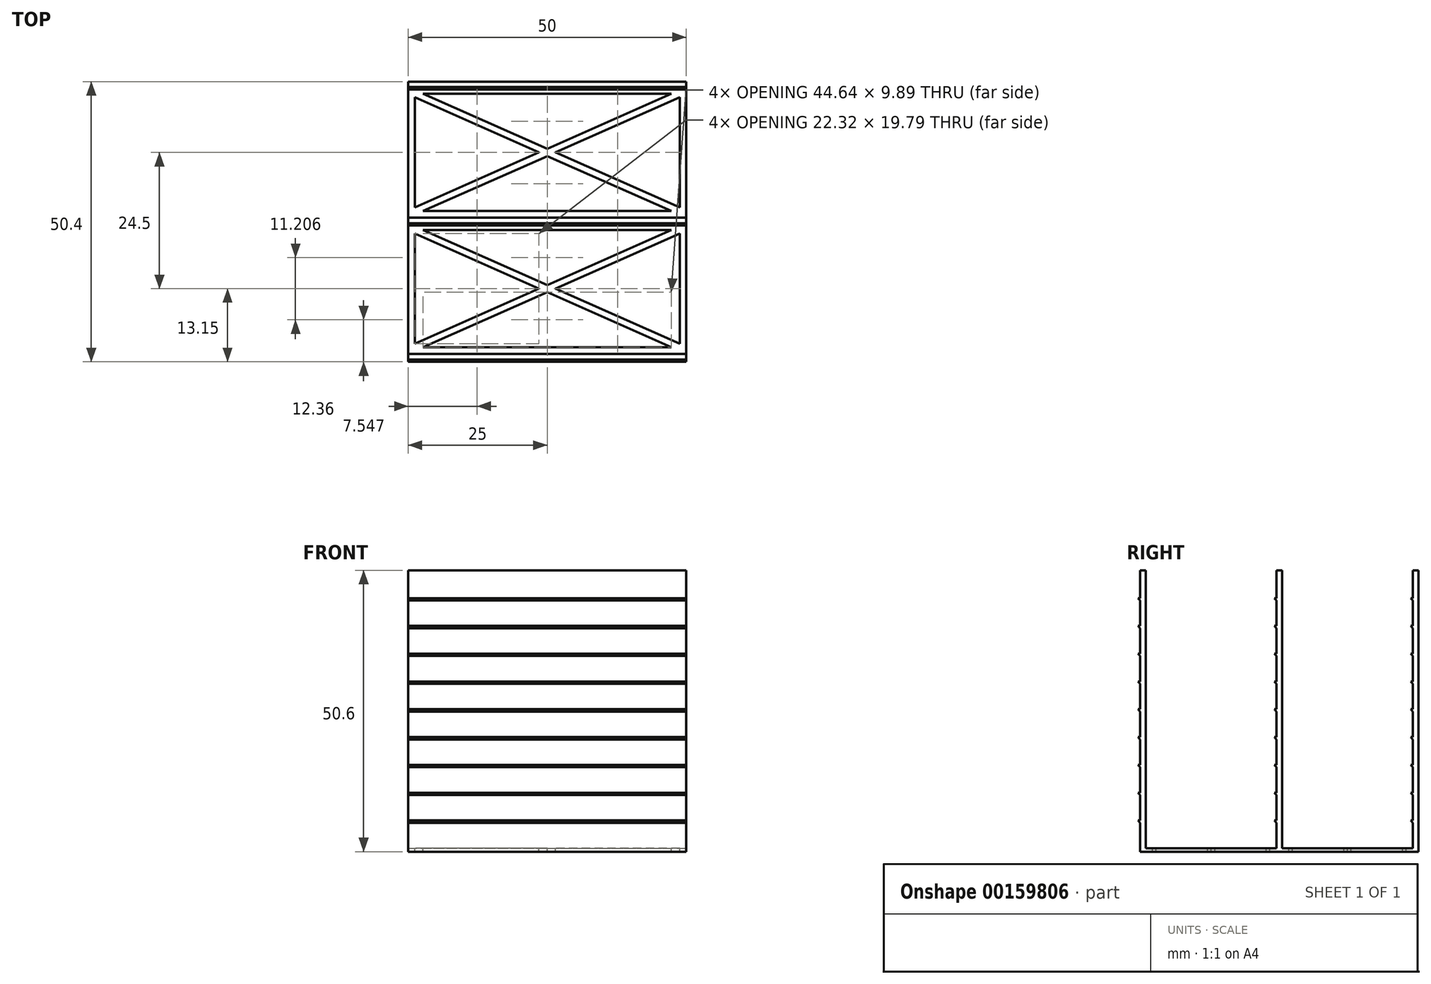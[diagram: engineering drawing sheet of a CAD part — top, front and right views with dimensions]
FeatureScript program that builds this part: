
annotation { "Feature Type Name" : "Feature", "Feature Type Description" : "" }
export const myFeature = defineFeature(function(context is Context, id is Id, definition is map)
    precondition{}
    {
        {
            var Q0;
            Q0=qCreatedBy(makeId("Top.planeOp"),FACE);
            var sketch = newSketch(context, id + "F0", { "sketchPlane" : qUnion([Q0])});
            skPoint(sketch, "E0.middle", {"position": v(0, 0) * mm});
            skLineSegment(sketch, "E1.bottom", {"start": v(-25, 25) * mm, "end": v(25, 25) * mm});
            skLineSegment(sketch, "E1.top", {"start": v(-25, 24) * mm, "end": v(25, 24) * mm});
            skLineSegment(sketch, "E1.left", {"start": v(-25, 25) * mm, "end": v(-25, 24) * mm});
            skLineSegment(sketch, "E1.right", {"start": v(25, 25) * mm, "end": v(25, 24) * mm});
            skPoint(sketch, "E1.middle", {"position": v(0, 24.5) * mm});
            skLineSegment(sketch, "E2.bottom", {"start": v(-25, 0.5) * mm, "end": v(25, 0.5) * mm});
            skLineSegment(sketch, "E2.top", {"start": v(-25, -0.5) * mm, "end": v(25, -0.5) * mm});
            skLineSegment(sketch, "E2.left", {"start": v(-25, 0.5) * mm, "end": v(-25, -0.5) * mm});
            skLineSegment(sketch, "E2.right", {"start": v(25, 0.5) * mm, "end": v(25, -0.5) * mm});
            skLineSegment(sketch, "E3.bottom", {"start": v(-25, -24) * mm, "end": v(25, -24) * mm});
            skLineSegment(sketch, "E3.top", {"start": v(-25, -25) * mm, "end": v(25, -25) * mm});
            skLineSegment(sketch, "E3.left", {"start": v(-25, -24) * mm, "end": v(-25, -25) * mm});
            skLineSegment(sketch, "E3.right", {"start": v(25, -24) * mm, "end": v(25, -25) * mm});
            skPoint(sketch, "E3.middle", {"position": v(0, -24.5) * mm});
            skLineSegment(sketch, "E4.left", {"start": v(-25, 25) * mm, "end": v(-25, -25) * mm});
            skLineSegment(sketch, "E4.right", {"start": v(25, 25) * mm, "end": v(25, -25) * mm});
            skLineSegment(sketch, "E5.bottom", {"start": v(-23.8, 22.8) * mm, "end": v(23.8, 22.8) * mm});
            skLineSegment(sketch, "E5.top", {"start": v(-23.8, 1.7) * mm, "end": v(23.8, 1.7) * mm});
            skLineSegment(sketch, "E5.left", {"start": v(-23.8, 22.8) * mm, "end": v(-23.8, 1.7) * mm});
            skLineSegment(sketch, "E5.right", {"start": v(23.8, 22.8) * mm, "end": v(23.8, 1.7) * mm});
            skLineSegment(sketch, "E6", {"start": v(-23.8, 22.8) * mm, "end": v(23.8, 1.7) * mm, "construction": true});
            skLineSegment(sketch, "E7", {"start": v(23.8, 22.8) * mm, "end": v(-23.8, 1.7) * mm, "construction": true});
            skLineSegment(sketch, "E8", {"start": v(-23.8, 22.8) * mm, "end": v(-25, 22.8) * mm, "construction": true});
            skLineSegment(sketch, "E9", {"start": v(-23.8, 22.8) * mm, "end": v(-23.8, 24) * mm, "construction": true});
            skLineSegment(sketch, "E10", {"start": v(-23.8, 1.7) * mm, "end": v(-23.8, 0.5) * mm, "construction": true});
            skLineSegment(sketch, "E11.0", {"start": v(-23.8, 22.14) * mm, "end": v(22.32, 1.7) * mm});
            skLineSegment(sketch, "E12.0", {"start": v(-22.32, 22.8) * mm, "end": v(23.8, 2.36) * mm});
            skLineSegment(sketch, "E13.0", {"start": v(22.32, 22.8) * mm, "end": v(-23.8, 2.36) * mm});
            skLineSegment(sketch, "E14.0", {"start": v(23.8, 22.14) * mm, "end": v(-22.32, 1.7) * mm});
            skLineSegment(sketch, "E15.MirrorCS", {"start": v(-23.8, -22.8) * mm, "end": v(-23.8, -1.7) * mm});
            skLineSegment(sketch, "E16.MirrorCS", {"start": v(-23.8, -1.7) * mm, "end": v(23.8, -1.7) * mm});
            skLineSegment(sketch, "E17.MirrorCS", {"start": v(23.8, -22.8) * mm, "end": v(23.8, -1.7) * mm});
            skLineSegment(sketch, "E18.MirrorCS", {"start": v(-23.8, -22.8) * mm, "end": v(23.8, -22.8) * mm});
            skLineSegment(sketch, "E19.MirrorCS", {"start": v(23.8, -22.14) * mm, "end": v(-22.32, -1.7) * mm});
            skLineSegment(sketch, "E20.MirrorCS", {"start": v(22.32, -22.8) * mm, "end": v(-23.8, -2.36) * mm});
            skLineSegment(sketch, "E21.MirrorCS", {"start": v(-22.32, -22.8) * mm, "end": v(23.8, -2.36) * mm});
            skLineSegment(sketch, "E22.MirrorCS", {"start": v(-23.8, -22.14) * mm, "end": v(22.32, -1.7) * mm});
            skSolve(sketch);
        }
        {
            var Q0;
            Q0=makeQuery(id+"F0.imprint","IMPRINT",FACE,{"disambiguationData":[TD([[makeQuery(id+"F0.imprint","IMPRINT",EDGE,{"derivedFrom":sQuery(id+"F0.wireOp",EDGE,"E0.bottom")}),1.0]])]});
            var Q1;
            Q1=makeQuery(id+"F0.imprint","IMPRINT",FACE,{"disambiguationData":[TD([[makeQuery(id+"F0.imprint","IMPRINT",EDGE,{"derivedFrom":sQuery(id+"F0.wireOp",EDGE,"QWfyO98P-nReG-di9y-126s-5mOLykfiqYH5")}),1.0]])]});
            var Q2;
            Q2=makeQuery(id+"F0.imprint","IMPRINT",FACE,{"disambiguationData":[TD([[makeQuery(id+"F0.imprint","IMPRINT",EDGE,{"derivedFrom":sQuery(id+"F0.wireOp",EDGE,"DmCEL1rD-3tOg-Wg76-rsYw-25NWHVf6hnsO")}),1.0]])]});
            var Q3;
            Q3=makeQuery(id+"F0.imprint","IMPRINT",FACE,{"disambiguationData":[TD([[makeQuery(id+"F0.imprint","IMPRINT",EDGE,{"derivedFrom":sQuery(id+"F0.wireOp",EDGE,"K1cKH9qt-eAHN-jujT-Ysw8-32v16pyBWlPN")}),1.0]])]});
            var Q4;
            Q4=makeQuery(id+"F0.imprint","IMPRINT",FACE,{"disambiguationData":[TD([[makeQuery(id+"F0.imprint","IMPRINT",EDGE,{"derivedFrom":sQuery(id+"F0.wireOp",EDGE,"bcf984ff-cba1-42ba-802e-a5a17bfec991.0.1.2")}),1.0]])]});
            var Q5;
            Q5=makeQuery(id+"F0.imprint","IMPRINT",FACE,{"disambiguationData":[TD([[makeQuery(id+"F0.imprint","IMPRINT",EDGE,{"derivedFrom":sQuery(id+"F0.wireOp",EDGE,"bcf984ff-cba1-42ba-802e-a5a17bfec991.0.1.1")}),1.0]])]});
            var Q6;
            Q6=makeQuery(id+"F0.imprint","IMPRINT",FACE,{"disambiguationData":[TD([[makeQuery(id+"F0.imprint","IMPRINT",EDGE,{"derivedFrom":sQuery(id+"F0.wireOp",EDGE,"bcf984ff-cba1-42ba-802e-a5a17bfec991.0.1.0")}),1.0]])]});
            var Q7;
            Q7=makeQuery(id+"F0.imprint","IMPRINT",FACE,{"disambiguationData":[TD([[makeQuery(id+"F0.imprint","IMPRINT",EDGE,{"derivedFrom":sQuery(id+"F0.wireOp",EDGE,"bcf984ff-cba1-42ba-802e-a5a17bfec991.0.2.0")}),1.0]])]});
            var Q8;
            Q8=makeQuery(id+"F0.imprint","IMPRINT",FACE,{"disambiguationData":[TD([[makeQuery(id+"F0.imprint","IMPRINT",EDGE,{"derivedFrom":sQuery(id+"F0.wireOp",EDGE,"bcf984ff-cba1-42ba-802e-a5a17bfec991.0.2.1")}),1.0]])]});
            var Q9;
            Q9=makeQuery(id+"F0.imprint","IMPRINT",FACE,{"disambiguationData":[TD([[makeQuery(id+"F0.imprint","IMPRINT",EDGE,{"derivedFrom":sQuery(id+"F0.wireOp",EDGE,"bcf984ff-cba1-42ba-802e-a5a17bfec991.0.2.2")}),1.0]])]});
            var Q10;
            {var subQ0=sQuery(id+"F0.wireOp",EDGE,"E1.top");Q10=makeQuery(id+"F0.imprint","IMPRINT",FACE,{"disambiguationData":[TD([[makeQuery(id+"F0.imprint","IMPRINT",EDGE,{"derivedFrom":subQ0}),-1.0]])]});}
            var Q11;
            {var subQ0=sQuery(id+"F0.wireOp",EDGE,"E2.top");Q11=makeQuery(id+"F0.imprint","IMPRINT",FACE,{"disambiguationData":[TD([[makeQuery(id+"F0.imprint","IMPRINT",EDGE,{"derivedFrom":subQ0}),-1.0]])]});}
            var Q12;
            {var subQ0=sQuery(id+"F0.wireOp",EDGE,"E3.bottom");Q12=makeQuery(id+"F0.imprint","IMPRINT",FACE,{"disambiguationData":[TD([[makeQuery(id+"F0.imprint","IMPRINT",EDGE,{"derivedFrom":subQ0}),-1.0]])]});}
            var Q13;
            {var subQ0=sQuery(id+"F0.wireOp",EDGE,"E2.bottom");Q13=makeQuery(id+"F0.imprint","IMPRINT",FACE,{"disambiguationData":[TD([[makeQuery(id+"F0.imprint","IMPRINT",EDGE,{"derivedFrom":subQ0}),-1.0]])]});}
            var Q14;
            {var subQ0=sQuery(id+"F0.wireOp",EDGE,"E1.top");Q14=makeQuery(id+"F0.imprint","IMPRINT",FACE,{"disambiguationData":[TD([[makeQuery(id+"F0.imprint","IMPRINT",EDGE,{"derivedFrom":subQ0}),1.0]])]});}
            var Q15;
            {var subQ1=sQuery(id+"F0.wireOp",EDGE,"E5.bottom");var subQ6=sQuery(id+"F0.wireOp",EDGE,"E5.left");var subQ9=makeQuery(id+"F0.imprint","INTERSECT",VERTEX,{"derivedFrom":[subQ1,subQ6]});Q15=makeQuery(id+"F0.imprint","IMPRINT",FACE,{"disambiguationData":[TD([[makeQuery(id+"F0.imprint","IMPRINT",EDGE,{"disambiguationData":[TD([[subQ9,-1.0]])],"derivedFrom":subQ1}),-1.0]])]});}
            var Q16;
            {var subQ1=sQuery(id+"F0.wireOp",EDGE,"E5.bottom");var subQ5=sQuery(id+"F0.wireOp",EDGE,"E5.right");var subQ6=makeQuery(id+"F0.imprint","INTERSECT",VERTEX,{"derivedFrom":[subQ1,subQ5]});Q16=makeQuery(id+"F0.imprint","IMPRINT",FACE,{"disambiguationData":[TD([[makeQuery(id+"F0.imprint","IMPRINT",EDGE,{"disambiguationData":[TD([[subQ6,1.0]])],"derivedFrom":subQ1}),-1.0]])]});}
            var Q17;
            {var subQ0=sQuery(id+"F0.wireOp",EDGE,"E13.0");var subQ1=sQuery(id+"F0.wireOp",EDGE,"E11.0");var subQ2=makeQuery(id+"F0.imprint","INTERSECT",VERTEX,{"derivedFrom":[subQ1,subQ0]});Q17=makeQuery(id+"F0.imprint","IMPRINT",FACE,{"disambiguationData":[TD([[makeQuery(id+"F0.imprint","IMPRINT",EDGE,{"disambiguationData":[TD([[subQ2,-1.0]])],"derivedFrom":subQ1}),1.0]])]});}
            var Q18;
            {var subQ1=sQuery(id+"F0.wireOp",EDGE,"E5.right");var subQ6=sQuery(id+"F0.wireOp",EDGE,"E5.top");var subQ9=makeQuery(id+"F0.imprint","INTERSECT",VERTEX,{"derivedFrom":[subQ6,subQ1]});Q18=makeQuery(id+"F0.imprint","IMPRINT",FACE,{"disambiguationData":[TD([[makeQuery(id+"F0.imprint","IMPRINT",EDGE,{"disambiguationData":[TD([[subQ9,1.0]])],"derivedFrom":subQ6}),1.0]])]});}
            var Q19;
            {var subQ5=sQuery(id+"F0.wireOp",EDGE,"E5.left");var subQ6=sQuery(id+"F0.wireOp",EDGE,"E5.top");var subQ7=makeQuery(id+"F0.imprint","INTERSECT",VERTEX,{"derivedFrom":[subQ6,subQ5]});Q19=makeQuery(id+"F0.imprint","IMPRINT",FACE,{"disambiguationData":[TD([[makeQuery(id+"F0.imprint","IMPRINT",EDGE,{"disambiguationData":[TD([[subQ7,-1.0]])],"derivedFrom":subQ6}),1.0]])]});}
            var Q20;
            {var subQ1=sQuery(id+"F0.wireOp",EDGE,"E16.MirrorCS");var subQ6=sQuery(id+"F0.wireOp",EDGE,"E15.MirrorCS");var subQ9=makeQuery(id+"F0.imprint","INTERSECT",VERTEX,{"derivedFrom":[subQ6,subQ1]});Q20=makeQuery(id+"F0.imprint","IMPRINT",FACE,{"disambiguationData":[TD([[makeQuery(id+"F0.imprint","IMPRINT",EDGE,{"disambiguationData":[TD([[subQ9,1.0]])],"derivedFrom":subQ6}),-1.0]])]});}
            var Q21;
            {var subQ0=sQuery(id+"F0.wireOp",EDGE,"E21.MirrorCS");var subQ1=sQuery(id+"F0.wireOp",EDGE,"E19.MirrorCS");var subQ2=makeQuery(id+"F0.imprint","INTERSECT",VERTEX,{"derivedFrom":[subQ1,subQ0]});Q21=makeQuery(id+"F0.imprint","IMPRINT",FACE,{"disambiguationData":[TD([[makeQuery(id+"F0.imprint","IMPRINT",EDGE,{"disambiguationData":[TD([[subQ2,-1.0]])],"derivedFrom":subQ1}),1.0]])]});}
            var Q22;
            {var subQ5=sQuery(id+"F0.wireOp",EDGE,"E17.MirrorCS");var subQ6=sQuery(id+"F0.wireOp",EDGE,"E16.MirrorCS");var subQ7=makeQuery(id+"F0.imprint","INTERSECT",VERTEX,{"derivedFrom":[subQ6,subQ5]});Q22=makeQuery(id+"F0.imprint","IMPRINT",FACE,{"disambiguationData":[TD([[makeQuery(id+"F0.imprint","IMPRINT",EDGE,{"disambiguationData":[TD([[subQ7,1.0]])],"derivedFrom":subQ6}),-1.0]])]});}
            var Q23;
            {var subQ1=sQuery(id+"F0.wireOp",EDGE,"E18.MirrorCS");var subQ6=sQuery(id+"F0.wireOp",EDGE,"E17.MirrorCS");var subQ9=makeQuery(id+"F0.imprint","INTERSECT",VERTEX,{"derivedFrom":[subQ6,subQ1]});Q23=makeQuery(id+"F0.imprint","IMPRINT",FACE,{"disambiguationData":[TD([[makeQuery(id+"F0.imprint","IMPRINT",EDGE,{"disambiguationData":[TD([[subQ9,-1.0]])],"derivedFrom":subQ6}),1.0]])]});}
            var Q24;
            {var subQ1=sQuery(id+"F0.wireOp",EDGE,"E18.MirrorCS");var subQ5=sQuery(id+"F0.wireOp",EDGE,"E15.MirrorCS");var subQ6=makeQuery(id+"F0.imprint","INTERSECT",VERTEX,{"derivedFrom":[subQ5,subQ1]});Q24=makeQuery(id+"F0.imprint","IMPRINT",FACE,{"disambiguationData":[TD([[makeQuery(id+"F0.imprint","IMPRINT",EDGE,{"disambiguationData":[TD([[subQ6,-1.0]])],"derivedFrom":subQ5}),-1.0]])]});}
            extrude(context, id + "F1", {"entities" : qUnion([Q0, Q1, Q2, Q3, Q4, Q5, Q6, Q7, Q8, Q9, Q10, Q11, Q12, Q13, Q14, Q15, Q16, Q17, Q18, Q19, Q20, Q21, Q22, Q23, Q24]), "oppositeDirection" : true, "depth" : 0.6 * mm});
        }
        {
            var Q0;
            Q0=makeQuery(id+"F0.imprint","IMPRINT",FACE,{"disambiguationData":[TD([[makeQuery(id+"F0.imprint","IMPRINT",EDGE,{"derivedFrom":sQuery(id+"F0.wireOp",EDGE,"QWfyO98P-nReG-di9y-126s-5mOLykfiqYH5")}),1.0]])]});
            var Q1;
            Q1=makeQuery(id+"F0.imprint","IMPRINT",FACE,{"disambiguationData":[TD([[makeQuery(id+"F0.imprint","IMPRINT",EDGE,{"derivedFrom":sQuery(id+"F0.wireOp",EDGE,"DmCEL1rD-3tOg-Wg76-rsYw-25NWHVf6hnsO")}),1.0]])]});
            var Q2;
            Q2=makeQuery(id+"F0.imprint","IMPRINT",FACE,{"disambiguationData":[TD([[makeQuery(id+"F0.imprint","IMPRINT",EDGE,{"derivedFrom":sQuery(id+"F0.wireOp",EDGE,"K1cKH9qt-eAHN-jujT-Ysw8-32v16pyBWlPN")}),1.0]])]});
            var Q3;
            Q3=makeQuery(id+"F0.imprint","IMPRINT",FACE,{"disambiguationData":[TD([[makeQuery(id+"F0.imprint","IMPRINT",EDGE,{"derivedFrom":sQuery(id+"F0.wireOp",EDGE,"bcf984ff-cba1-42ba-802e-a5a17bfec991.0.1.2")}),1.0]])]});
            var Q4;
            Q4=makeQuery(id+"F0.imprint","IMPRINT",FACE,{"disambiguationData":[TD([[makeQuery(id+"F0.imprint","IMPRINT",EDGE,{"derivedFrom":sQuery(id+"F0.wireOp",EDGE,"bcf984ff-cba1-42ba-802e-a5a17bfec991.0.1.1")}),1.0]])]});
            var Q5;
            Q5=makeQuery(id+"F0.imprint","IMPRINT",FACE,{"disambiguationData":[TD([[makeQuery(id+"F0.imprint","IMPRINT",EDGE,{"derivedFrom":sQuery(id+"F0.wireOp",EDGE,"bcf984ff-cba1-42ba-802e-a5a17bfec991.0.1.0")}),1.0]])]});
            var Q6;
            Q6=makeQuery(id+"F0.imprint","IMPRINT",FACE,{"disambiguationData":[TD([[makeQuery(id+"F0.imprint","IMPRINT",EDGE,{"derivedFrom":sQuery(id+"F0.wireOp",EDGE,"bcf984ff-cba1-42ba-802e-a5a17bfec991.0.2.0")}),1.0]])]});
            var Q7;
            Q7=makeQuery(id+"F0.imprint","IMPRINT",FACE,{"disambiguationData":[TD([[makeQuery(id+"F0.imprint","IMPRINT",EDGE,{"derivedFrom":sQuery(id+"F0.wireOp",EDGE,"bcf984ff-cba1-42ba-802e-a5a17bfec991.0.2.1")}),1.0]])]});
            var Q8;
            Q8=makeQuery(id+"F0.imprint","IMPRINT",FACE,{"disambiguationData":[TD([[makeQuery(id+"F0.imprint","IMPRINT",EDGE,{"derivedFrom":sQuery(id+"F0.wireOp",EDGE,"bcf984ff-cba1-42ba-802e-a5a17bfec991.0.2.2")}),1.0]])]});
            var Q9;
            {var subQ0=sQuery(id+"F0.wireOp",EDGE,"E1.top");Q9=makeQuery(id+"F0.imprint","IMPRINT",FACE,{"disambiguationData":[TD([[makeQuery(id+"F0.imprint","IMPRINT",EDGE,{"derivedFrom":subQ0}),1.0]])]});}
            var Q10;
            {var subQ0=sQuery(id+"F0.wireOp",EDGE,"E2.bottom");Q10=makeQuery(id+"F0.imprint","IMPRINT",FACE,{"disambiguationData":[TD([[makeQuery(id+"F0.imprint","IMPRINT",EDGE,{"derivedFrom":subQ0}),-1.0]])]});}
            var Q11;
            {var subQ0=sQuery(id+"F0.wireOp",EDGE,"E3.bottom");Q11=makeQuery(id+"F0.imprint","IMPRINT",FACE,{"disambiguationData":[TD([[makeQuery(id+"F0.imprint","IMPRINT",EDGE,{"derivedFrom":subQ0}),-1.0]])]});}
            extrude(context, id + "F2", {"entities" : qUnion([Q0, Q1, Q2, Q3, Q4, Q5, Q6, Q7, Q8, Q9, Q10, Q11]), "operationType" : NewBodyOperationType.ADD, "depth" : 50 * mm});
        }
        {
            var Q0;
            {var subQ0=sQuery(id+"F0.wireOp",EDGE,"E4.left");Q0=makeQuery(id+"F2.boolean.opBoolean","MERGE",FACE,{"derivedFrom":[makeQuery(id+"F1.opExtrude","SWEPT_FACE",FACE,{"disambiguationData":[OSD([subQ0])]}),makeQuery(id+"F2.opExtrude","SWEPT_FACE",FACE,{"disambiguationData":[OSD([subQ0]),TDD([makeQuery(id+"F0.imprint","IMPRINT",EDGE,{"disambiguationData":[TD([[makeQuery(id+"F0.imprint","INTERSECT",VERTEX,{"derivedFrom":[sQuery(id+"F0.wireOp",EDGE,"E1.top"),subQ0]}),1.0]])],"derivedFrom":subQ0})])]}),makeQuery(id+"F2.opExtrude","SWEPT_FACE",FACE,{"disambiguationData":[OSD([subQ0]),TDD([makeQuery(id+"F0.imprint","IMPRINT",EDGE,{"disambiguationData":[TD([[makeQuery(id+"F0.imprint","INTERSECT",VERTEX,{"derivedFrom":[sQuery(id+"F0.wireOp",EDGE,"E2.bottom"),subQ0]}),-1.0]])],"derivedFrom":subQ0})])]}),makeQuery(id+"F2.opExtrude","SWEPT_FACE",FACE,{"disambiguationData":[OSD([subQ0]),TDD([makeQuery(id+"F0.imprint","IMPRINT",EDGE,{"disambiguationData":[TD([[makeQuery(id+"F0.imprint","INTERSECT",VERTEX,{"derivedFrom":[sQuery(id+"F0.wireOp",EDGE,"E3.bottom"),subQ0]}),-1.0]])],"derivedFrom":subQ0})])]})]});}
            var sketch = newSketch(context, id + "F3", { "sketchPlane" : qUnion([Q0])});
            skLineSegment(sketch, "E23", {"start": v(-24, 4.6) * mm, "end": v(-23.6, 5) * mm});
            skLineSegment(sketch, "E24", {"start": v(-23.6, 5) * mm, "end": v(-24, 5) * mm});
            skLineSegment(sketch, "E25", {"start": v(-24, 5) * mm, "end": v(-24, 4.6) * mm});
            skLineSegment(sketch, "E26", {"start": v(0.5, 5) * mm, "end": v(0.9, 5) * mm});
            skLineSegment(sketch, "E27", {"start": v(0.9, 5) * mm, "end": v(0.5, 4.6) * mm});
            skLineSegment(sketch, "E28", {"start": v(0.5, 4.6) * mm, "end": v(0.5, 5) * mm});
            skLineSegment(sketch, "E29", {"start": v(25, 5) * mm, "end": v(25.4, 5) * mm});
            skLineSegment(sketch, "E30", {"start": v(25.4, 5) * mm, "end": v(25, 4.6) * mm});
            skLineSegment(sketch, "E31", {"start": v(25, 4.6) * mm, "end": v(25, 5) * mm});
            skLineSegment(sketch, "E32.0.1.0", {"start": v(25, 10) * mm, "end": v(25.4, 10) * mm});
            skLineSegment(sketch, "E32.0.1.1", {"start": v(25.4, 10) * mm, "end": v(25, 9.6) * mm});
            skLineSegment(sketch, "E32.0.1.2", {"start": v(0.5, 10) * mm, "end": v(0.9, 10) * mm});
            skLineSegment(sketch, "E32.0.1.3", {"start": v(0.5, 9.6) * mm, "end": v(0.5, 10) * mm});
            skLineSegment(sketch, "E32.0.1.4", {"start": v(0.9, 10) * mm, "end": v(0.5, 9.6) * mm});
            skLineSegment(sketch, "E32.0.1.5", {"start": v(25, 9.6) * mm, "end": v(25, 10) * mm});
            skLineSegment(sketch, "E32.0.1.6", {"start": v(-24, 10) * mm, "end": v(-24, 9.6) * mm});
            skLineSegment(sketch, "E32.0.1.7", {"start": v(-23.6, 10) * mm, "end": v(-24, 10) * mm});
            skLineSegment(sketch, "E32.0.1.8", {"start": v(-24, 9.6) * mm, "end": v(-23.6, 10) * mm});
            skLineSegment(sketch, "E32.0.2.0", {"start": v(25, 15) * mm, "end": v(25.4, 15) * mm});
            skLineSegment(sketch, "E32.0.2.1", {"start": v(25.4, 15) * mm, "end": v(25, 14.6) * mm});
            skLineSegment(sketch, "E32.0.2.2", {"start": v(0.5, 15) * mm, "end": v(0.9, 15) * mm});
            skLineSegment(sketch, "E32.0.2.3", {"start": v(0.5, 14.6) * mm, "end": v(0.5, 15) * mm});
            skLineSegment(sketch, "E32.0.2.4", {"start": v(0.9, 15) * mm, "end": v(0.5, 14.6) * mm});
            skLineSegment(sketch, "E32.0.2.5", {"start": v(25, 14.6) * mm, "end": v(25, 15) * mm});
            skLineSegment(sketch, "E32.0.2.6", {"start": v(-24, 15) * mm, "end": v(-24, 14.6) * mm});
            skLineSegment(sketch, "E32.0.2.7", {"start": v(-23.6, 15) * mm, "end": v(-24, 15) * mm});
            skLineSegment(sketch, "E32.0.2.8", {"start": v(-24, 14.6) * mm, "end": v(-23.6, 15) * mm});
            skLineSegment(sketch, "E32.0.3.0", {"start": v(25, 20) * mm, "end": v(25.4, 20) * mm});
            skLineSegment(sketch, "E32.0.3.1", {"start": v(25.4, 20) * mm, "end": v(25, 19.6) * mm});
            skLineSegment(sketch, "E32.0.3.2", {"start": v(0.5, 20) * mm, "end": v(0.9, 20) * mm});
            skLineSegment(sketch, "E32.0.3.3", {"start": v(0.5, 19.6) * mm, "end": v(0.5, 20) * mm});
            skLineSegment(sketch, "E32.0.3.4", {"start": v(0.9, 20) * mm, "end": v(0.5, 19.6) * mm});
            skLineSegment(sketch, "E32.0.3.5", {"start": v(25, 19.6) * mm, "end": v(25, 20) * mm});
            skLineSegment(sketch, "E32.0.3.6", {"start": v(-24, 20) * mm, "end": v(-24, 19.6) * mm});
            skLineSegment(sketch, "E32.0.3.7", {"start": v(-23.6, 20) * mm, "end": v(-24, 20) * mm});
            skLineSegment(sketch, "E32.0.3.8", {"start": v(-24, 19.6) * mm, "end": v(-23.6, 20) * mm});
            skLineSegment(sketch, "E32.0.4.0", {"start": v(25, 25) * mm, "end": v(25.4, 25) * mm});
            skLineSegment(sketch, "E32.0.4.1", {"start": v(25.4, 25) * mm, "end": v(25, 24.6) * mm});
            skLineSegment(sketch, "E32.0.4.2", {"start": v(0.5, 25) * mm, "end": v(0.9, 25) * mm});
            skLineSegment(sketch, "E32.0.4.3", {"start": v(0.5, 24.6) * mm, "end": v(0.5, 25) * mm});
            skLineSegment(sketch, "E32.0.4.4", {"start": v(0.9, 25) * mm, "end": v(0.5, 24.6) * mm});
            skLineSegment(sketch, "E32.0.4.5", {"start": v(25, 24.6) * mm, "end": v(25, 25) * mm});
            skLineSegment(sketch, "E32.0.4.6", {"start": v(-24, 25) * mm, "end": v(-24, 24.6) * mm});
            skLineSegment(sketch, "E32.0.4.7", {"start": v(-23.6, 25) * mm, "end": v(-24, 25) * mm});
            skLineSegment(sketch, "E32.0.4.8", {"start": v(-24, 24.6) * mm, "end": v(-23.6, 25) * mm});
            skLineSegment(sketch, "E32.0.5.0", {"start": v(25, 30) * mm, "end": v(25.4, 30) * mm});
            skLineSegment(sketch, "E32.0.5.1", {"start": v(25.4, 30) * mm, "end": v(25, 29.6) * mm});
            skLineSegment(sketch, "E32.0.5.2", {"start": v(0.5, 30) * mm, "end": v(0.9, 30) * mm});
            skLineSegment(sketch, "E32.0.5.3", {"start": v(0.5, 29.6) * mm, "end": v(0.5, 30) * mm});
            skLineSegment(sketch, "E32.0.5.4", {"start": v(0.9, 30) * mm, "end": v(0.5, 29.6) * mm});
            skLineSegment(sketch, "E32.0.5.5", {"start": v(25, 29.6) * mm, "end": v(25, 30) * mm});
            skLineSegment(sketch, "E32.0.5.6", {"start": v(-24, 30) * mm, "end": v(-24, 29.6) * mm});
            skLineSegment(sketch, "E32.0.5.7", {"start": v(-23.6, 30) * mm, "end": v(-24, 30) * mm});
            skLineSegment(sketch, "E32.0.5.8", {"start": v(-24, 29.6) * mm, "end": v(-23.6, 30) * mm});
            skLineSegment(sketch, "E32.0.6.0", {"start": v(25, 35) * mm, "end": v(25.4, 35) * mm});
            skLineSegment(sketch, "E32.0.6.1", {"start": v(25.4, 35) * mm, "end": v(25, 34.6) * mm});
            skLineSegment(sketch, "E32.0.6.2", {"start": v(0.5, 35) * mm, "end": v(0.9, 35) * mm});
            skLineSegment(sketch, "E32.0.6.3", {"start": v(0.5, 34.6) * mm, "end": v(0.5, 35) * mm});
            skLineSegment(sketch, "E32.0.6.4", {"start": v(0.9, 35) * mm, "end": v(0.5, 34.6) * mm});
            skLineSegment(sketch, "E32.0.6.5", {"start": v(25, 34.6) * mm, "end": v(25, 35) * mm});
            skLineSegment(sketch, "E32.0.6.6", {"start": v(-24, 35) * mm, "end": v(-24, 34.6) * mm});
            skLineSegment(sketch, "E32.0.6.7", {"start": v(-23.6, 35) * mm, "end": v(-24, 35) * mm});
            skLineSegment(sketch, "E32.0.6.8", {"start": v(-24, 34.6) * mm, "end": v(-23.6, 35) * mm});
            skLineSegment(sketch, "E32.0.7.0", {"start": v(25, 40) * mm, "end": v(25.4, 40) * mm});
            skLineSegment(sketch, "E32.0.7.1", {"start": v(25.4, 40) * mm, "end": v(25, 39.6) * mm});
            skLineSegment(sketch, "E32.0.7.2", {"start": v(0.5, 40) * mm, "end": v(0.9, 40) * mm});
            skLineSegment(sketch, "E32.0.7.3", {"start": v(0.5, 39.6) * mm, "end": v(0.5, 40) * mm});
            skLineSegment(sketch, "E32.0.7.4", {"start": v(0.9, 40) * mm, "end": v(0.5, 39.6) * mm});
            skLineSegment(sketch, "E32.0.7.5", {"start": v(25, 39.6) * mm, "end": v(25, 40) * mm});
            skLineSegment(sketch, "E32.0.7.6", {"start": v(-24, 40) * mm, "end": v(-24, 39.6) * mm});
            skLineSegment(sketch, "E32.0.7.7", {"start": v(-23.6, 40) * mm, "end": v(-24, 40) * mm});
            skLineSegment(sketch, "E32.0.7.8", {"start": v(-24, 39.6) * mm, "end": v(-23.6, 40) * mm});
            skLineSegment(sketch, "E32.0.8.0", {"start": v(25, 45) * mm, "end": v(25.4, 45) * mm});
            skLineSegment(sketch, "E32.0.8.1", {"start": v(25.4, 45) * mm, "end": v(25, 44.6) * mm});
            skLineSegment(sketch, "E32.0.8.2", {"start": v(0.5, 45) * mm, "end": v(0.9, 45) * mm});
            skLineSegment(sketch, "E32.0.8.3", {"start": v(0.5, 44.6) * mm, "end": v(0.5, 45) * mm});
            skLineSegment(sketch, "E32.0.8.4", {"start": v(0.9, 45) * mm, "end": v(0.5, 44.6) * mm});
            skLineSegment(sketch, "E32.0.8.5", {"start": v(25, 44.6) * mm, "end": v(25, 45) * mm});
            skLineSegment(sketch, "E32.0.8.6", {"start": v(-24, 45) * mm, "end": v(-24, 44.6) * mm});
            skLineSegment(sketch, "E32.0.8.7", {"start": v(-23.6, 45) * mm, "end": v(-24, 45) * mm});
            skLineSegment(sketch, "E32.0.8.8", {"start": v(-24, 44.6) * mm, "end": v(-23.6, 45) * mm});
            skLineSegment(sketch, "E32.direction1", {"start": v(-24, 4.6) * mm, "end": v(1, 4.6) * mm, "construction": true});
            skLineSegment(sketch, "E32.direction2", {"start": v(-24, 4.6) * mm, "end": v(-24, 9.6) * mm, "construction": true});
            skSolve(sketch);
        }
        {
            var Q0;
            Q0=makeQuery(id+"F3.imprint","IMPRINT",FACE,{"disambiguationData":[TD([[makeQuery(id+"F3.imprint","IMPRINT",EDGE,{"derivedFrom":sQuery(id+"F3.wireOp",EDGE,"E32.0.8.6")}),1.0]])]});
            var Q1;
            Q1=makeQuery(id+"F3.imprint","IMPRINT",FACE,{"disambiguationData":[TD([[makeQuery(id+"F3.imprint","IMPRINT",EDGE,{"derivedFrom":sQuery(id+"F3.wireOp",EDGE,"E32.0.7.6")}),1.0]])]});
            var Q2;
            Q2=makeQuery(id+"F3.imprint","IMPRINT",FACE,{"disambiguationData":[TD([[makeQuery(id+"F3.imprint","IMPRINT",EDGE,{"derivedFrom":sQuery(id+"F3.wireOp",EDGE,"E32.0.6.6")}),1.0]])]});
            var Q3;
            Q3=makeQuery(id+"F3.imprint","IMPRINT",FACE,{"disambiguationData":[TD([[makeQuery(id+"F3.imprint","IMPRINT",EDGE,{"derivedFrom":sQuery(id+"F3.wireOp",EDGE,"E32.0.5.6")}),1.0]])]});
            var Q4;
            Q4=makeQuery(id+"F3.imprint","IMPRINT",FACE,{"disambiguationData":[TD([[makeQuery(id+"F3.imprint","IMPRINT",EDGE,{"derivedFrom":sQuery(id+"F3.wireOp",EDGE,"E32.0.4.6")}),1.0]])]});
            var Q5;
            Q5=makeQuery(id+"F3.imprint","IMPRINT",FACE,{"disambiguationData":[TD([[makeQuery(id+"F3.imprint","IMPRINT",EDGE,{"derivedFrom":sQuery(id+"F3.wireOp",EDGE,"E32.0.3.6")}),1.0]])]});
            var Q6;
            Q6=makeQuery(id+"F3.imprint","IMPRINT",FACE,{"disambiguationData":[TD([[makeQuery(id+"F3.imprint","IMPRINT",EDGE,{"derivedFrom":sQuery(id+"F3.wireOp",EDGE,"E32.0.2.6")}),1.0]])]});
            var Q7;
            Q7=makeQuery(id+"F3.imprint","IMPRINT",FACE,{"disambiguationData":[TD([[makeQuery(id+"F3.imprint","IMPRINT",EDGE,{"derivedFrom":sQuery(id+"F3.wireOp",EDGE,"E32.0.1.6")}),1.0]])]});
            var Q8;
            Q8=makeQuery(id+"F3.imprint","IMPRINT",FACE,{"disambiguationData":[TD([[makeQuery(id+"F3.imprint","IMPRINT",EDGE,{"derivedFrom":sQuery(id+"F3.wireOp",EDGE,"E23")}),1.0]])]});
            var Q9;
            Q9=makeQuery(id+"F3.imprint","IMPRINT",FACE,{"disambiguationData":[TD([[makeQuery(id+"F3.imprint","IMPRINT",EDGE,{"derivedFrom":sQuery(id+"F3.wireOp",EDGE,"E26")}),-1.0]])]});
            var Q10;
            Q10=makeQuery(id+"F3.imprint","IMPRINT",FACE,{"disambiguationData":[TD([[makeQuery(id+"F3.imprint","IMPRINT",EDGE,{"derivedFrom":sQuery(id+"F3.wireOp",EDGE,"E32.0.1.2")}),-1.0]])]});
            var Q11;
            Q11=makeQuery(id+"F3.imprint","IMPRINT",FACE,{"disambiguationData":[TD([[makeQuery(id+"F3.imprint","IMPRINT",EDGE,{"derivedFrom":sQuery(id+"F3.wireOp",EDGE,"E32.0.2.2")}),-1.0]])]});
            var Q12;
            Q12=makeQuery(id+"F3.imprint","IMPRINT",FACE,{"disambiguationData":[TD([[makeQuery(id+"F3.imprint","IMPRINT",EDGE,{"derivedFrom":sQuery(id+"F3.wireOp",EDGE,"E32.0.3.2")}),-1.0]])]});
            var Q13;
            Q13=makeQuery(id+"F3.imprint","IMPRINT",FACE,{"disambiguationData":[TD([[makeQuery(id+"F3.imprint","IMPRINT",EDGE,{"derivedFrom":sQuery(id+"F3.wireOp",EDGE,"E32.0.4.2")}),-1.0]])]});
            var Q14;
            Q14=makeQuery(id+"F3.imprint","IMPRINT",FACE,{"disambiguationData":[TD([[makeQuery(id+"F3.imprint","IMPRINT",EDGE,{"derivedFrom":sQuery(id+"F3.wireOp",EDGE,"E32.0.5.2")}),-1.0]])]});
            var Q15;
            Q15=makeQuery(id+"F3.imprint","IMPRINT",FACE,{"disambiguationData":[TD([[makeQuery(id+"F3.imprint","IMPRINT",EDGE,{"derivedFrom":sQuery(id+"F3.wireOp",EDGE,"E32.0.6.2")}),-1.0]])]});
            var Q16;
            Q16=makeQuery(id+"F3.imprint","IMPRINT",FACE,{"disambiguationData":[TD([[makeQuery(id+"F3.imprint","IMPRINT",EDGE,{"derivedFrom":sQuery(id+"F3.wireOp",EDGE,"E32.0.7.2")}),-1.0]])]});
            var Q17;
            Q17=makeQuery(id+"F3.imprint","IMPRINT",FACE,{"disambiguationData":[TD([[makeQuery(id+"F3.imprint","IMPRINT",EDGE,{"derivedFrom":sQuery(id+"F3.wireOp",EDGE,"E32.0.8.2")}),-1.0]])]});
            var Q18;
            Q18=makeQuery(id+"F3.imprint","IMPRINT",FACE,{"disambiguationData":[TD([[makeQuery(id+"F3.imprint","IMPRINT",EDGE,{"derivedFrom":sQuery(id+"F3.wireOp",EDGE,"E32.0.8.0")}),-1.0]])]});
            var Q19;
            Q19=makeQuery(id+"F3.imprint","IMPRINT",FACE,{"disambiguationData":[TD([[makeQuery(id+"F3.imprint","IMPRINT",EDGE,{"derivedFrom":sQuery(id+"F3.wireOp",EDGE,"E32.0.7.0")}),-1.0]])]});
            var Q20;
            Q20=makeQuery(id+"F3.imprint","IMPRINT",FACE,{"disambiguationData":[TD([[makeQuery(id+"F3.imprint","IMPRINT",EDGE,{"derivedFrom":sQuery(id+"F3.wireOp",EDGE,"E32.0.6.0")}),-1.0]])]});
            var Q21;
            Q21=makeQuery(id+"F3.imprint","IMPRINT",FACE,{"disambiguationData":[TD([[makeQuery(id+"F3.imprint","IMPRINT",EDGE,{"derivedFrom":sQuery(id+"F3.wireOp",EDGE,"E32.0.5.0")}),-1.0]])]});
            var Q22;
            Q22=makeQuery(id+"F3.imprint","IMPRINT",FACE,{"disambiguationData":[TD([[makeQuery(id+"F3.imprint","IMPRINT",EDGE,{"derivedFrom":sQuery(id+"F3.wireOp",EDGE,"E32.0.4.0")}),-1.0]])]});
            var Q23;
            Q23=makeQuery(id+"F3.imprint","IMPRINT",FACE,{"disambiguationData":[TD([[makeQuery(id+"F3.imprint","IMPRINT",EDGE,{"derivedFrom":sQuery(id+"F3.wireOp",EDGE,"E32.0.3.0")}),-1.0]])]});
            var Q24;
            Q24=makeQuery(id+"F3.imprint","IMPRINT",FACE,{"disambiguationData":[TD([[makeQuery(id+"F3.imprint","IMPRINT",EDGE,{"derivedFrom":sQuery(id+"F3.wireOp",EDGE,"E32.0.2.0")}),-1.0]])]});
            var Q25;
            Q25=makeQuery(id+"F3.imprint","IMPRINT",FACE,{"disambiguationData":[TD([[makeQuery(id+"F3.imprint","IMPRINT",EDGE,{"derivedFrom":sQuery(id+"F3.wireOp",EDGE,"E32.0.1.0")}),-1.0]])]});
            var Q26;
            Q26=makeQuery(id+"F3.imprint","IMPRINT",FACE,{"disambiguationData":[TD([[makeQuery(id+"F3.imprint","IMPRINT",EDGE,{"derivedFrom":sQuery(id+"F3.wireOp",EDGE,"E29")}),-1.0]])]});
            var Q27;
            {var subQ0=sQuery(id+"F0.wireOp",EDGE,"E4.right");Q27=makeQuery(id+"F2.boolean.opBoolean","MERGE",FACE,{"derivedFrom":[makeQuery(id+"F1.opExtrude","SWEPT_FACE",FACE,{"disambiguationData":[OSD([subQ0])]}),makeQuery(id+"F2.opExtrude","SWEPT_FACE",FACE,{"disambiguationData":[OSD([subQ0]),TDD([makeQuery(id+"F0.imprint","IMPRINT",EDGE,{"disambiguationData":[TD([[makeQuery(id+"F0.imprint","INTERSECT",VERTEX,{"derivedFrom":[sQuery(id+"F0.wireOp",EDGE,"E1.top"),subQ0]}),1.0]])],"derivedFrom":subQ0})])]}),makeQuery(id+"F2.opExtrude","SWEPT_FACE",FACE,{"disambiguationData":[OSD([subQ0]),TDD([makeQuery(id+"F0.imprint","IMPRINT",EDGE,{"disambiguationData":[TD([[makeQuery(id+"F0.imprint","INTERSECT",VERTEX,{"derivedFrom":[sQuery(id+"F0.wireOp",EDGE,"E2.bottom"),subQ0]}),-1.0]])],"derivedFrom":subQ0})])]}),makeQuery(id+"F2.opExtrude","SWEPT_FACE",FACE,{"disambiguationData":[OSD([subQ0]),TDD([makeQuery(id+"F0.imprint","IMPRINT",EDGE,{"disambiguationData":[TD([[makeQuery(id+"F0.imprint","INTERSECT",VERTEX,{"derivedFrom":[sQuery(id+"F0.wireOp",EDGE,"E3.bottom"),subQ0]}),-1.0]])],"derivedFrom":subQ0})])]})]});}
            extrude(context, id + "F4", {"entities" : qUnion([Q0, Q1, Q2, Q3, Q4, Q5, Q6, Q7, Q8, Q9, Q10, Q11, Q12, Q13, Q14, Q15, Q16, Q17, Q18, Q19, Q20, Q21, Q22, Q23, Q24, Q25, Q26]), "operationType" : NewBodyOperationType.ADD, "endBound" : BoundingType.UP_TO_SURFACE, "oppositeDirection" : true, "endBoundEntityFace" : qUnion([Q27]), "depth" : 25 * mm});
        }
    });
